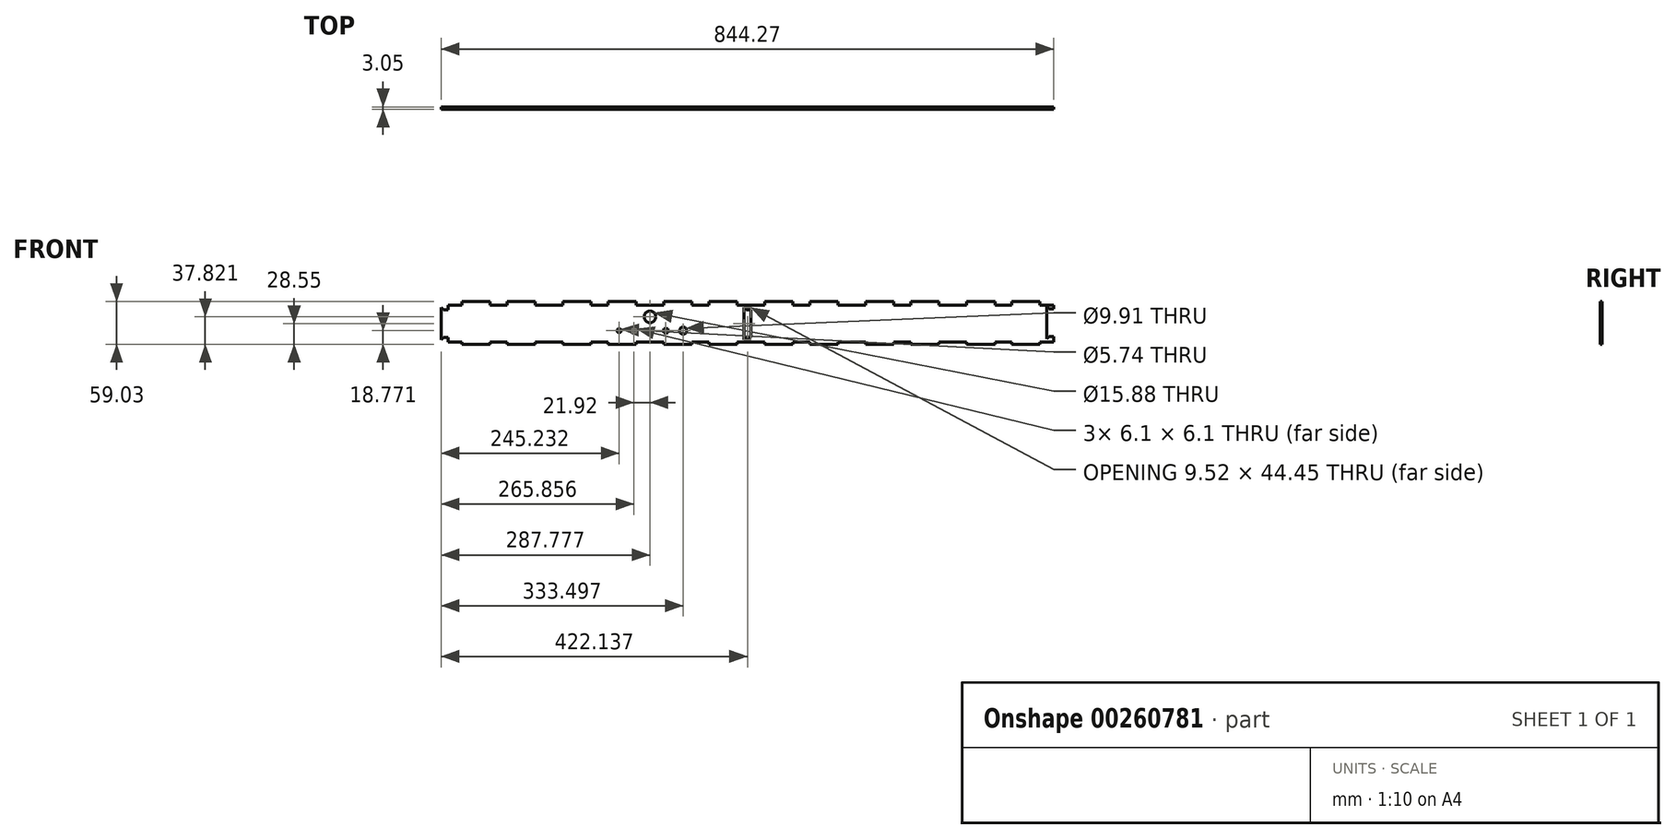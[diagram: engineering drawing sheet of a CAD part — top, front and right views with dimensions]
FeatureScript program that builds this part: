
annotation { "Feature Type Name" : "Feature", "Feature Type Description" : "" }
export const myFeature = defineFeature(function(context is Context, id is Id, definition is map)
    precondition{}
    {
        {
            var Q0;
            Q0=qCreatedBy(makeId("Front.planeOp"),FACE);
            var sketch = newSketch(context, id + "F0", { "sketchPlane" : qUnion([Q0])});
            skLineSegment(sketch, "E0.bottom", {"start": v(0, 0) * mm, "end": v(834.74, 0) * mm});
            skLineSegment(sketch, "E0.top", {"start": v(0, 50.8) * mm, "end": v(834.74, 50.8) * mm});
            skLineSegment(sketch, "E0.left", {"start": v(0, 0) * mm, "end": v(0, 50.8) * mm});
            skLineSegment(sketch, "E0.right", {"start": v(834.74, 0) * mm, "end": v(834.74, 50.8) * mm});
            skLineSegment(sketch, "E1", {"start": v(57.92, 50.8) * mm, "end": v(57.92, 0) * mm, "construction": true});
            skLineSegment(sketch, "E2", {"start": v(75.88, 50.8) * mm, "end": v(75.88, 0) * mm, "construction": true});
            skLineSegment(sketch, "E3", {"start": v(776.82, 50.8) * mm, "end": v(776.82, 0) * mm, "construction": true});
            skLineSegment(sketch, "E4", {"start": v(758.86, 50.8) * mm, "end": v(758.86, 0) * mm, "construction": true});
            skSolve(sketch);
        }
        {
            var Q0;
            Q0=makeQuery(id+"F0.imprint","IMPRINT",FACE,{"disambiguationData":[TD([[makeQuery(id+"F0.imprint","IMPRINT",EDGE,{"derivedFrom":sQuery(id+"F0.wireOp",EDGE,"E0.bottom")}),1.0]])]});
            extrude(context, id + "F1", {"entities" : qUnion([Q0]), "depth" : 3.05 * mm});
        }
        {
            var Q0;
            Q0=makeQuery(id+"F1.opExtrude","CAP_FACE",FACE,{"disambiguationData":[OSD([sQuery(id+"F0.wireOp",EDGE,"E0.bottom"),sQuery(id+"F0.wireOp",EDGE,"E0.top"),sQuery(id+"F0.wireOp",EDGE,"E0.left"),sQuery(id+"F0.wireOp",EDGE,"E0.right")])],"isStart":false});
            var sketch = newSketch(context, id + "F2", { "sketchPlane" : qUnion([Q0])});
            skLineSegment(sketch, "E5", {"start": v(57.92, 0) * mm, "end": v(57.92, 50.8) * mm});
            skLineSegment(sketch, "E6", {"start": v(81.2, 0) * mm, "end": v(81.2, 50.8) * mm});
            skLineSegment(sketch, "E7", {"start": v(776.82, 0) * mm, "end": v(776.82, 50.8) * mm});
            skLineSegment(sketch, "E8", {"start": v(753.54, 0) * mm, "end": v(753.54, 50.8) * mm});
            skLineSegment(sketch, "E9", {"start": v(197.05, 50.8) * mm, "end": v(197.05, 0) * mm});
            skLineSegment(sketch, "E10", {"start": v(220.32, 0) * mm, "end": v(220.32, 50.8) * mm});
            skLineSegment(sketch, "E11", {"start": v(336.17, 50.8) * mm, "end": v(336.17, 0) * mm});
            skLineSegment(sketch, "E12", {"start": v(359.45, 0.94) * mm, "end": v(359.45, 50.8) * mm});
            skLineSegment(sketch, "E13", {"start": v(475.3, 0) * mm, "end": v(475.3, 50.8) * mm});
            skLineSegment(sketch, "E14", {"start": v(498.57, 0) * mm, "end": v(498.57, 50.8) * mm});
            skLineSegment(sketch, "E15", {"start": v(614.42, 50.8) * mm, "end": v(614.42, 0) * mm});
            skLineSegment(sketch, "E16", {"start": v(637.7, 50.8) * mm, "end": v(637.7, 0) * mm});
            skCircle(sketch, "E17", {"center": v(9.53, 25.4) * mm, "radius": 1.27 * mm});
            skPoint(sketch, "E17.centerSnap0", {"position": v(0, 25.4) * mm});
            skCircle(sketch, "E18", {"center": v(825.22, 25.4) * mm, "radius": 1.27 * mm});
            skSolve(sketch);
        }
        {
            var Q0;
            {var subQ0=sQuery(id+"F2.wireOp",EDGE,"E6");Q0=makeQuery(id+"F2.imprint","IMPRINT",FACE,{"disambiguationData":[TD([[makeQuery(id+"F2.imprint","IMPRINT",EDGE,{"derivedFrom":subQ0}),-1.0]])]});}
            var sketch = newSketch(context, id + "F3", { "sketchPlane" : qUnion([Q0])});
            skLineSegment(sketch, "E19", {"start": v(0, 25.4) * mm, "end": v(834.74, 25.4) * mm, "construction": true});
            skLineSegment(sketch, "E20", {"start": v(0, 50.8) * mm, "end": v(0, 55.88) * mm});
            skLineSegment(sketch, "E21", {"start": v(0, 55.88) * mm, "end": v(57.92, 55.88) * mm});
            skLineSegment(sketch, "E22", {"start": v(57.92, 55.88) * mm, "end": v(57.92, 50.8) * mm});
            skLineSegment(sketch, "E23", {"start": v(81.2, 50.8) * mm, "end": v(81.2, 55.88) * mm});
            skLineSegment(sketch, "E24", {"start": v(81.2, 55.88) * mm, "end": v(197.05, 55.88) * mm});
            skLineSegment(sketch, "E25", {"start": v(197.05, 55.88) * mm, "end": v(197.05, 50.8) * mm});
            skLineSegment(sketch, "E26", {"start": v(220.32, 50.8) * mm, "end": v(220.32, 55.88) * mm});
            skLineSegment(sketch, "E27", {"start": v(220.32, 55.88) * mm, "end": v(336.17, 55.88) * mm});
            skLineSegment(sketch, "E28", {"start": v(336.17, 55.88) * mm, "end": v(336.17, 50.8) * mm});
            skLineSegment(sketch, "E29", {"start": v(359.45, 50.8) * mm, "end": v(359.45, 55.88) * mm});
            skLineSegment(sketch, "E30", {"start": v(359.45, 55.88) * mm, "end": v(475.3, 55.88) * mm});
            skLineSegment(sketch, "E31", {"start": v(475.3, 55.88) * mm, "end": v(475.3, 50.8) * mm});
            skLineSegment(sketch, "E32", {"start": v(498.57, 50.8) * mm, "end": v(498.57, 55.88) * mm});
            skLineSegment(sketch, "E33", {"start": v(498.57, 55.88) * mm, "end": v(614.42, 55.88) * mm});
            skLineSegment(sketch, "E34", {"start": v(614.42, 55.88) * mm, "end": v(614.42, 50.8) * mm});
            skLineSegment(sketch, "E35", {"start": v(637.7, 50.8) * mm, "end": v(637.7, 55.88) * mm});
            skLineSegment(sketch, "E36", {"start": v(637.7, 55.88) * mm, "end": v(753.54, 55.88) * mm});
            skLineSegment(sketch, "E37", {"start": v(753.54, 55.88) * mm, "end": v(753.54, 50.8) * mm});
            skLineSegment(sketch, "E38", {"start": v(776.82, 50.8) * mm, "end": v(776.82, 55.88) * mm});
            skLineSegment(sketch, "E39", {"start": v(776.82, 55.88) * mm, "end": v(834.74, 55.88) * mm});
            skLineSegment(sketch, "E40", {"start": v(834.74, 55.88) * mm, "end": v(834.74, 50.8) * mm});
            skLineSegment(sketch, "E41", {"start": v(0, 50.8) * mm, "end": v(834.74, 50.8) * mm});
            skLineSegment(sketch, "E42.bottom", {"start": v(0, 0) * mm, "end": v(57.92, 0) * mm});
            skLineSegment(sketch, "E42.top", {"start": v(0, -3.15) * mm, "end": v(57.92, -3.15) * mm});
            skLineSegment(sketch, "E42.left", {"start": v(0, 0) * mm, "end": v(0, -3.15) * mm});
            skLineSegment(sketch, "E42.right", {"start": v(57.92, 0) * mm, "end": v(57.92, -3.15) * mm});
            skLineSegment(sketch, "E43.bottom", {"start": v(81.2, 0) * mm, "end": v(197.05, 0) * mm});
            skLineSegment(sketch, "E43.top", {"start": v(81.2, -3.15) * mm, "end": v(197.05, -3.15) * mm});
            skLineSegment(sketch, "E43.left", {"start": v(81.2, 0) * mm, "end": v(81.2, -3.15) * mm});
            skLineSegment(sketch, "E43.right", {"start": v(197.05, 0) * mm, "end": v(197.05, -3.15) * mm});
            skLineSegment(sketch, "E44.bottom", {"start": v(220.32, 0) * mm, "end": v(336.17, 0) * mm});
            skLineSegment(sketch, "E44.top", {"start": v(220.32, -3.15) * mm, "end": v(336.17, -3.15) * mm});
            skLineSegment(sketch, "E44.left", {"start": v(220.32, 0) * mm, "end": v(220.32, -3.15) * mm});
            skLineSegment(sketch, "E44.right", {"start": v(336.17, 0) * mm, "end": v(336.17, -3.15) * mm});
            skLineSegment(sketch, "E45.bottom", {"start": v(359.45, 0) * mm, "end": v(475.3, 0) * mm});
            skLineSegment(sketch, "E45.top", {"start": v(359.45, -3.15) * mm, "end": v(475.3, -3.15) * mm});
            skLineSegment(sketch, "E45.left", {"start": v(359.45, 0) * mm, "end": v(359.45, -3.15) * mm});
            skLineSegment(sketch, "E45.right", {"start": v(475.3, 0) * mm, "end": v(475.3, -3.15) * mm});
            skLineSegment(sketch, "E46.bottom", {"start": v(498.57, 0) * mm, "end": v(614.42, 0) * mm});
            skLineSegment(sketch, "E46.top", {"start": v(498.57, -3.15) * mm, "end": v(614.42, -3.15) * mm});
            skLineSegment(sketch, "E46.left", {"start": v(498.57, 0) * mm, "end": v(498.57, -3.15) * mm});
            skLineSegment(sketch, "E46.right", {"start": v(614.42, 0) * mm, "end": v(614.42, -3.15) * mm});
            skLineSegment(sketch, "E47.bottom", {"start": v(637.7, 0) * mm, "end": v(753.54, 0) * mm});
            skLineSegment(sketch, "E47.top", {"start": v(637.7, -3.15) * mm, "end": v(753.54, -3.15) * mm});
            skLineSegment(sketch, "E47.left", {"start": v(637.7, 0) * mm, "end": v(637.7, -3.15) * mm});
            skLineSegment(sketch, "E47.right", {"start": v(753.54, 0) * mm, "end": v(753.54, -3.15) * mm});
            skLineSegment(sketch, "E48.bottom", {"start": v(776.82, 0) * mm, "end": v(834.74, 0) * mm});
            skLineSegment(sketch, "E48.top", {"start": v(776.82, -3.15) * mm, "end": v(834.74, -3.15) * mm});
            skLineSegment(sketch, "E48.left", {"start": v(776.82, 0) * mm, "end": v(776.82, -3.15) * mm});
            skLineSegment(sketch, "E48.right", {"start": v(834.74, 0) * mm, "end": v(834.74, -3.15) * mm});
            skSolve(sketch);
        }
        {
            var Q0;
            {var subQ0=sQuery(id+"F3.wireOp",EDGE,"E20");Q0=makeQuery(id+"F3.imprint","IMPRINT",FACE,{"disambiguationData":[TD([[makeQuery(id+"F3.imprint","IMPRINT",EDGE,{"derivedFrom":subQ0}),-1.0]])]});}
            var Q1;
            {var subQ0=sQuery(id+"F3.wireOp",EDGE,"E23");Q1=makeQuery(id+"F3.imprint","IMPRINT",FACE,{"disambiguationData":[TD([[makeQuery(id+"F3.imprint","IMPRINT",EDGE,{"derivedFrom":subQ0}),-1.0]])]});}
            var Q2;
            {var subQ0=sQuery(id+"F3.wireOp",EDGE,"300d203a-4e24-4113-8f0b-c0bd62af7ee03.MirrorCS");Q2=makeQuery(id+"F3.imprint","IMPRINT",FACE,{"disambiguationData":[TD([[makeQuery(id+"F3.imprint","IMPRINT",EDGE,{"derivedFrom":subQ0}),1.0]])]});}
            var Q3;
            {var subQ0=sQuery(id+"F3.wireOp",EDGE,"300d203a-4e24-4113-8f0b-c0bd62af7ee06.MirrorCS");Q3=makeQuery(id+"F3.imprint","IMPRINT",FACE,{"disambiguationData":[TD([[makeQuery(id+"F3.imprint","IMPRINT",EDGE,{"derivedFrom":subQ0}),1.0]])]});}
            var Q4;
            {var subQ0=sQuery(id+"F3.wireOp",EDGE,"E26");Q4=makeQuery(id+"F3.imprint","IMPRINT",FACE,{"disambiguationData":[TD([[makeQuery(id+"F3.imprint","IMPRINT",EDGE,{"derivedFrom":subQ0}),-1.0]])]});}
            var Q5;
            {var subQ0=sQuery(id+"F3.wireOp",EDGE,"300d203a-4e24-4113-8f0b-c0bd62af7ee09.MirrorCS");Q5=makeQuery(id+"F3.imprint","IMPRINT",FACE,{"disambiguationData":[TD([[makeQuery(id+"F3.imprint","IMPRINT",EDGE,{"derivedFrom":subQ0}),1.0]])]});}
            var Q6;
            {var subQ0=sQuery(id+"F3.wireOp",EDGE,"E29");Q6=makeQuery(id+"F3.imprint","IMPRINT",FACE,{"disambiguationData":[TD([[makeQuery(id+"F3.imprint","IMPRINT",EDGE,{"derivedFrom":subQ0}),-1.0]])]});}
            var Q7;
            {var subQ0=sQuery(id+"F3.wireOp",EDGE,"300d203a-4e24-4113-8f0b-c0bd62af7ee05.MirrorCS");Q7=makeQuery(id+"F3.imprint","IMPRINT",FACE,{"disambiguationData":[TD([[makeQuery(id+"F3.imprint","IMPRINT",EDGE,{"derivedFrom":subQ0}),1.0]])]});}
            var Q8;
            {var subQ0=sQuery(id+"F3.wireOp",EDGE,"E32");Q8=makeQuery(id+"F3.imprint","IMPRINT",FACE,{"disambiguationData":[TD([[makeQuery(id+"F3.imprint","IMPRINT",EDGE,{"derivedFrom":subQ0}),-1.0]])]});}
            var Q9;
            {var subQ0=sQuery(id+"F3.wireOp",EDGE,"300d203a-4e24-4113-8f0b-c0bd62af7ee02.MirrorCS");Q9=makeQuery(id+"F3.imprint","IMPRINT",FACE,{"disambiguationData":[TD([[makeQuery(id+"F3.imprint","IMPRINT",EDGE,{"derivedFrom":subQ0}),1.0]])]});}
            var Q10;
            {var subQ0=sQuery(id+"F3.wireOp",EDGE,"E35");Q10=makeQuery(id+"F3.imprint","IMPRINT",FACE,{"disambiguationData":[TD([[makeQuery(id+"F3.imprint","IMPRINT",EDGE,{"derivedFrom":subQ0}),-1.0]])]});}
            var Q11;
            {var subQ0=sQuery(id+"F3.wireOp",EDGE,"300d203a-4e24-4113-8f0b-c0bd62af7ee00.MirrorCS");Q11=makeQuery(id+"F3.imprint","IMPRINT",FACE,{"disambiguationData":[TD([[makeQuery(id+"F3.imprint","IMPRINT",EDGE,{"derivedFrom":subQ0}),1.0]])]});}
            var Q12;
            {var subQ0=sQuery(id+"F3.wireOp",EDGE,"E38");Q12=makeQuery(id+"F3.imprint","IMPRINT",FACE,{"disambiguationData":[TD([[makeQuery(id+"F3.imprint","IMPRINT",EDGE,{"derivedFrom":subQ0}),-1.0]])]});}
            var Q13;
            {var subQ0=sQuery(id+"F3.wireOp",EDGE,"300d203a-4e24-4113-8f0b-c0bd62af7ee04.MirrorCS");Q13=makeQuery(id+"F3.imprint","IMPRINT",FACE,{"disambiguationData":[TD([[makeQuery(id+"F3.imprint","IMPRINT",EDGE,{"derivedFrom":subQ0}),1.0]])]});}
            var Q14;
            Q14=makeQuery(id+"F3.imprint","IMPRINT",FACE,{"disambiguationData":[TD([[makeQuery(id+"F3.imprint","IMPRINT",EDGE,{"derivedFrom":sQuery(id+"F3.wireOp",EDGE,"E42.bottom")}),-1.0]])]});
            var Q15;
            Q15=makeQuery(id+"F3.imprint","IMPRINT",FACE,{"disambiguationData":[TD([[makeQuery(id+"F3.imprint","IMPRINT",EDGE,{"derivedFrom":sQuery(id+"F3.wireOp",EDGE,"E43.bottom")}),-1.0]])]});
            var Q16;
            Q16=makeQuery(id+"F3.imprint","IMPRINT",FACE,{"disambiguationData":[TD([[makeQuery(id+"F3.imprint","IMPRINT",EDGE,{"derivedFrom":sQuery(id+"F3.wireOp",EDGE,"E44.bottom")}),-1.0]])]});
            var Q17;
            Q17=makeQuery(id+"F3.imprint","IMPRINT",FACE,{"disambiguationData":[TD([[makeQuery(id+"F3.imprint","IMPRINT",EDGE,{"derivedFrom":sQuery(id+"F3.wireOp",EDGE,"E45.bottom")}),-1.0]])]});
            var Q18;
            Q18=makeQuery(id+"F3.imprint","IMPRINT",FACE,{"disambiguationData":[TD([[makeQuery(id+"F3.imprint","IMPRINT",EDGE,{"derivedFrom":sQuery(id+"F3.wireOp",EDGE,"E46.bottom")}),-1.0]])]});
            var Q19;
            Q19=makeQuery(id+"F3.imprint","IMPRINT",FACE,{"disambiguationData":[TD([[makeQuery(id+"F3.imprint","IMPRINT",EDGE,{"derivedFrom":sQuery(id+"F3.wireOp",EDGE,"E47.bottom")}),-1.0]])]});
            var Q20;
            Q20=makeQuery(id+"F3.imprint","IMPRINT",FACE,{"disambiguationData":[TD([[makeQuery(id+"F3.imprint","IMPRINT",EDGE,{"derivedFrom":sQuery(id+"F3.wireOp",EDGE,"E48.bottom")}),-1.0]])]});
            extrude(context, id + "F4", {"entities" : qUnion([Q0, Q1, Q2, Q3, Q4, Q5, Q6, Q7, Q8, Q9, Q10, Q11, Q12, Q13, Q14, Q15, Q16, Q17, Q18, Q19, Q20]), "operationType" : NewBodyOperationType.ADD, "oppositeDirection" : true, "depth" : 3.05 * mm});
        }
        {
            var Q0;
            {var subQ0=sQuery(id+"F2.wireOp",EDGE,"E6");Q0=makeQuery(id+"F2.imprint","IMPRINT",FACE,{"disambiguationData":[TD([[makeQuery(id+"F2.imprint","IMPRINT",EDGE,{"derivedFrom":subQ0}),-1.0]])]});}
            var sketch = newSketch(context, id + "F5", { "sketchPlane" : qUnion([Q0])});
            skLineSegment(sketch, "E49", {"start": v(0, 6.35) * mm, "end": v(0, 44.45) * mm});
            skPoint(sketch, "E50", {"position": v(0, 25.4) * mm});
            skLineSegment(sketch, "E51", {"start": v(0, 44.45) * mm, "end": v(-6.35, 44.45) * mm});
            skLineSegment(sketch, "E52", {"start": v(0, 6.35) * mm, "end": v(-6.35, 6.35) * mm});
            skLineSegment(sketch, "E53", {"start": v(-6.35, 44.45) * mm, "end": v(-9.52, 47.63) * mm});
            skLineSegment(sketch, "E54", {"start": v(-6.35, 6.35) * mm, "end": v(-9.52, 3.18) * mm});
            skLineSegment(sketch, "E55", {"start": v(-9.52, 47.63) * mm, "end": v(-9.52, 3.18) * mm});
            skLineSegment(sketch, "E56", {"start": v(834.74, 7.32) * mm, "end": v(834.74, 45.42) * mm});
            skPoint(sketch, "E57", {"position": v(834.74, 26.37) * mm});
            skLineSegment(sketch, "E58", {"start": v(834.74, 45.42) * mm, "end": v(828.4, 45.42) * mm});
            skLineSegment(sketch, "E59", {"start": v(834.74, 7.32) * mm, "end": v(828.4, 7.32) * mm});
            skLineSegment(sketch, "E60", {"start": v(828.4, 45.42) * mm, "end": v(825.22, 48.6) * mm});
            skLineSegment(sketch, "E61", {"start": v(828.4, 7.32) * mm, "end": v(825.22, 4.14) * mm});
            skLineSegment(sketch, "E62", {"start": v(825.22, 48.6) * mm, "end": v(825.22, 4.14) * mm});
            skSolve(sketch);
        }
        {
            var Q0;
            Q0=makeQuery(id+"F5.imprint","IMPRINT",FACE,{"disambiguationData":[TD([[makeQuery(id+"F5.imprint","IMPRINT",EDGE,{"derivedFrom":sQuery(id+"F5.wireOp",EDGE,"E49")}),1.0]])]});
            extrude(context, id + "F6", {"entities" : qUnion([Q0]), "operationType" : NewBodyOperationType.ADD, "oppositeDirection" : true, "depth" : 3.05 * mm});
        }
        {
            var Q0;
            Q0=makeQuery(id+"F5.imprint","IMPRINT",FACE,{"disambiguationData":[TD([[makeQuery(id+"F5.imprint","IMPRINT",EDGE,{"derivedFrom":sQuery(id+"F5.wireOp",EDGE,"E56")}),1.0]])]});
            extrude(context, id + "F7", {"entities" : qUnion([Q0]), "operationType" : NewBodyOperationType.REMOVE, "endBound" : BoundingType.THROUGH_ALL, "oppositeDirection" : true, "depth" : 25.4 * mm});
        }
        {
            var Q0;
            {var subQ0=sQuery(id+"F2.wireOp",EDGE,"E11");Q0=makeQuery(id+"F2.imprint","IMPRINT",FACE,{"disambiguationData":[TD([[makeQuery(id+"F2.imprint","IMPRINT",EDGE,{"derivedFrom":subQ0}),1.0]])]});}
            var sketch = newSketch(context, id + "F8", { "sketchPlane" : qUnion([Q0])});
            skLineSegment(sketch, "E63", {"start": v(417.37, 6.35) * mm, "end": v(417.37, 44.45) * mm});
            skLineSegment(sketch, "E64", {"start": v(417.37, 44.45) * mm, "end": v(411.02, 44.45) * mm});
            skLineSegment(sketch, "E65", {"start": v(411.02, 44.45) * mm, "end": v(407.85, 47.63) * mm});
            skLineSegment(sketch, "E66", {"start": v(407.85, 47.63) * mm, "end": v(407.85, 3.18) * mm});
            skLineSegment(sketch, "E67", {"start": v(407.85, 3.17) * mm, "end": v(411.02, 6.35) * mm});
            skLineSegment(sketch, "E68", {"start": v(411.02, 6.35) * mm, "end": v(417.37, 6.35) * mm});
            skPoint(sketch, "E69", {"position": v(417.37, 25.4) * mm});
            skPoint(sketch, "E70", {"position": v(407.85, 25.4) * mm});
            skLineSegment(sketch, "E71", {"start": v(407.85, 25.4) * mm, "end": v(417.37, 25.4) * mm, "construction": true});
            skSolve(sketch);
        }
        {
            var Q0;
            {var subQ0=sQuery(id+"F2.wireOp",EDGE,"E10");Q0=makeQuery(id+"F2.imprint","IMPRINT",FACE,{"disambiguationData":[TD([[makeQuery(id+"F2.imprint","IMPRINT",EDGE,{"derivedFrom":subQ0}),-1.0]])]});}
            var sketch = newSketch(context, id + "F9", { "sketchPlane" : qUnion([Q0])});
            skLineSegment(sketch, "E72.bottom", {"start": v(245.23, 21.59) * mm, "end": v(311.27, 21.59) * mm, "construction": true});
            skLineSegment(sketch, "E72.top", {"start": v(245.23, 9.65) * mm, "end": v(311.27, 9.65) * mm, "construction": true});
            skLineSegment(sketch, "E72.left", {"start": v(245.23, 21.59) * mm, "end": v(245.23, 9.65) * mm, "construction": true});
            skLineSegment(sketch, "E72.right", {"start": v(311.27, 21.59) * mm, "end": v(311.27, 9.65) * mm, "construction": true});
            skPoint(sketch, "E73", {"position": v(278.25, 9.65) * mm});
            skLineSegment(sketch, "E74.bottom", {"start": v(253.28, 12.57) * mm, "end": v(259.37, 12.57) * mm});
            skLineSegment(sketch, "E74.top", {"start": v(253.28, 18.67) * mm, "end": v(259.37, 18.67) * mm});
            skLineSegment(sketch, "E74.left", {"start": v(253.28, 12.57) * mm, "end": v(253.28, 18.67) * mm});
            skLineSegment(sketch, "E74.right", {"start": v(259.37, 12.57) * mm, "end": v(259.37, 18.67) * mm});
            skLineSegment(sketch, "E75.bottom", {"start": v(275.2, 12.57) * mm, "end": v(281.3, 12.57) * mm});
            skLineSegment(sketch, "E75.top", {"start": v(275.2, 18.67) * mm, "end": v(281.3, 18.67) * mm});
            skLineSegment(sketch, "E75.left", {"start": v(275.2, 12.57) * mm, "end": v(275.2, 18.67) * mm});
            skLineSegment(sketch, "E75.right", {"start": v(281.3, 12.57) * mm, "end": v(281.3, 18.67) * mm});
            skLineSegment(sketch, "E76.bottom", {"start": v(297.12, 12.57) * mm, "end": v(303.21, 12.57) * mm});
            skLineSegment(sketch, "E76.top", {"start": v(297.12, 18.67) * mm, "end": v(303.21, 18.67) * mm});
            skLineSegment(sketch, "E76.left", {"start": v(297.12, 12.57) * mm, "end": v(297.12, 18.67) * mm});
            skLineSegment(sketch, "E76.right", {"start": v(303.21, 12.57) * mm, "end": v(303.21, 18.67) * mm});
            skPoint(sketch, "E77", {"position": v(253.28, 15.62) * mm});
            skPoint(sketch, "E78", {"position": v(245.23, 15.62) * mm});
            skPoint(sketch, "E79", {"position": v(278.25, 18.67) * mm});
            skPoint(sketch, "E80", {"position": v(275.2, 15.62) * mm});
            skPoint(sketch, "E81", {"position": v(297.12, 15.62) * mm});
            skPoint(sketch, "E82", {"position": v(300.17, 18.67) * mm});
            skCircle(sketch, "E83", {"center": v(235.7, 15.62) * mm, "radius": 2.87 * mm});
            skCircle(sketch, "E84", {"center": v(323.97, 15.62) * mm, "radius": 4.95 * mm});
            skCircle(sketch, "E85", {"center": v(278.25, 34.67) * mm, "radius": 7.94 * mm});
            skSolve(sketch);
        }
        {
            var Q0;
            Q0=qSketchRegion(id+"F9",true);
            extrude(context, id + "F10", {"entities" : qUnion([Q0]), "operationType" : NewBodyOperationType.REMOVE, "endBound" : BoundingType.THROUGH_ALL, "oppositeDirection" : true, "depth" : 25.4 * mm});
        }
        {
            var Q0;
            Q0 = qSketchRegion(id + "F8", true);
            extrude(context, id + "F11", {"entities" : qUnion([Q0]), "operationType" : NewBodyOperationType.REMOVE, "oppositeDirection" : true, "depth" : 25.4 * mm});
        }
        {
            var Q0;
            {var subQ0=sQuery(id+"F2.wireOp",EDGE,"E6");Q0=makeQuery(id+"F2.imprint","IMPRINT",FACE,{"disambiguationData":[TD([[makeQuery(id+"F2.imprint","IMPRINT",EDGE,{"derivedFrom":subQ0}),-1.0]])]});}
            var sketch = newSketch(context, id + "F12", { "sketchPlane" : qUnion([Q0])});
            skLineSegment(sketch, "E86.bottom", {"start": v(158.17, -3.15) * mm, "end": v(120.07, -3.15) * mm});
            skLineSegment(sketch, "E86.top", {"start": v(158.17, -0.1) * mm, "end": v(120.07, -0.1) * mm});
            skLineSegment(sketch, "E86.left", {"start": v(158.17, -3.15) * mm, "end": v(158.17, -0.1) * mm});
            skLineSegment(sketch, "E86.right", {"start": v(120.07, -3.15) * mm, "end": v(120.07, -0.1) * mm});
            skLineSegment(sketch, "E87.bottom", {"start": v(259.2, -3.15) * mm, "end": v(297.3, -3.15) * mm});
            skLineSegment(sketch, "E87.top", {"start": v(259.2, -0.1) * mm, "end": v(297.3, -0.1) * mm});
            skLineSegment(sketch, "E87.left", {"start": v(259.2, -3.15) * mm, "end": v(259.2, -0.1) * mm});
            skLineSegment(sketch, "E87.right", {"start": v(297.3, -3.15) * mm, "end": v(297.3, -0.1) * mm});
            skLineSegment(sketch, "E88.bottom", {"start": v(398.32, -3.15) * mm, "end": v(436.42, -3.15) * mm});
            skLineSegment(sketch, "E88.top", {"start": v(398.32, -0.1) * mm, "end": v(436.42, -0.1) * mm});
            skLineSegment(sketch, "E88.left", {"start": v(398.32, -3.15) * mm, "end": v(398.32, -0.1) * mm});
            skLineSegment(sketch, "E88.right", {"start": v(436.42, -3.15) * mm, "end": v(436.42, -0.1) * mm});
            skLineSegment(sketch, "E89.bottom", {"start": v(537.44, -3.15) * mm, "end": v(575.54, -3.15) * mm});
            skLineSegment(sketch, "E89.top", {"start": v(537.44, -0.1) * mm, "end": v(575.54, -0.1) * mm});
            skLineSegment(sketch, "E89.left", {"start": v(537.44, -3.15) * mm, "end": v(537.44, -0.1) * mm});
            skLineSegment(sketch, "E89.right", {"start": v(575.54, -3.15) * mm, "end": v(575.54, -0.1) * mm});
            skLineSegment(sketch, "E90.bottom", {"start": v(676.57, -3.15) * mm, "end": v(714.67, -3.15) * mm});
            skLineSegment(sketch, "E90.top", {"start": v(676.57, -0.1) * mm, "end": v(714.67, -0.1) * mm});
            skLineSegment(sketch, "E90.left", {"start": v(676.57, -3.15) * mm, "end": v(676.57, -0.1) * mm});
            skLineSegment(sketch, "E90.right", {"start": v(714.67, -3.15) * mm, "end": v(714.67, -0.1) * mm});
            skLineSegment(sketch, "E91.bottom", {"start": v(815.7, -3.15) * mm, "end": v(853.8, -3.15) * mm});
            skLineSegment(sketch, "E91.top", {"start": v(815.7, -0.1) * mm, "end": v(853.8, -0.1) * mm});
            skLineSegment(sketch, "E91.left", {"start": v(815.7, -3.15) * mm, "end": v(815.7, -0.1) * mm});
            skLineSegment(sketch, "E91.right", {"start": v(853.8, -3.15) * mm, "end": v(853.8, -0.1) * mm});
            skLineSegment(sketch, "E92.bottom", {"start": v(19.05, -3.15) * mm, "end": v(-19.05, -3.15) * mm});
            skLineSegment(sketch, "E92.top", {"start": v(19.05, -0.1) * mm, "end": v(-19.05, -0.1) * mm});
            skLineSegment(sketch, "E92.left", {"start": v(19.05, -3.15) * mm, "end": v(19.05, -0.1) * mm});
            skLineSegment(sketch, "E92.right", {"start": v(-19.05, -3.15) * mm, "end": v(-19.05, -0.1) * mm});
            skPoint(sketch, "E93", {"position": v(139.12, -3.15) * mm});
            skPoint(sketch, "E94", {"position": v(278.25, -3.15) * mm});
            skPoint(sketch, "E95", {"position": v(417.37, -3.15) * mm});
            skPoint(sketch, "E96", {"position": v(556.5, -3.15) * mm});
            skPoint(sketch, "E97", {"position": v(695.62, -3.15) * mm});
            skPoint(sketch, "E98", {"position": v(0, -3.15) * mm});
            skPoint(sketch, "E99", {"position": v(834.74, -3.15) * mm});
            skLineSegment(sketch, "E100.bottom", {"start": v(-19.05, 55.88) * mm, "end": v(19.05, 55.88) * mm});
            skLineSegment(sketch, "E100.top", {"start": v(-19.05, 50.8) * mm, "end": v(19.05, 50.8) * mm});
            skLineSegment(sketch, "E100.left", {"start": v(-19.05, 55.88) * mm, "end": v(-19.05, 50.8) * mm});
            skLineSegment(sketch, "E100.right", {"start": v(19.05, 55.88) * mm, "end": v(19.05, 50.8) * mm});
            skLineSegment(sketch, "E101.bottom", {"start": v(120.07, 55.88) * mm, "end": v(158.17, 55.88) * mm});
            skLineSegment(sketch, "E101.top", {"start": v(120.07, 50.8) * mm, "end": v(158.17, 50.8) * mm});
            skLineSegment(sketch, "E101.left", {"start": v(120.07, 55.88) * mm, "end": v(120.07, 50.8) * mm});
            skLineSegment(sketch, "E101.right", {"start": v(158.17, 55.88) * mm, "end": v(158.17, 50.8) * mm});
            skLineSegment(sketch, "E102.bottom", {"start": v(259.2, 55.88) * mm, "end": v(297.3, 55.88) * mm});
            skLineSegment(sketch, "E102.top", {"start": v(259.2, 50.8) * mm, "end": v(297.3, 50.8) * mm});
            skLineSegment(sketch, "E102.left", {"start": v(259.2, 55.88) * mm, "end": v(259.2, 50.8) * mm});
            skLineSegment(sketch, "E102.right", {"start": v(297.3, 55.88) * mm, "end": v(297.3, 50.8) * mm});
            skLineSegment(sketch, "E103.bottom", {"start": v(398.32, 55.88) * mm, "end": v(436.42, 55.88) * mm});
            skLineSegment(sketch, "E103.top", {"start": v(398.32, 50.8) * mm, "end": v(436.42, 50.8) * mm});
            skLineSegment(sketch, "E103.left", {"start": v(398.32, 55.88) * mm, "end": v(398.32, 50.8) * mm});
            skLineSegment(sketch, "E103.right", {"start": v(436.42, 55.88) * mm, "end": v(436.42, 50.8) * mm});
            skLineSegment(sketch, "E104.bottom", {"start": v(537.44, 55.88) * mm, "end": v(575.54, 55.88) * mm});
            skLineSegment(sketch, "E104.top", {"start": v(537.44, 50.8) * mm, "end": v(575.54, 50.8) * mm});
            skLineSegment(sketch, "E104.left", {"start": v(537.44, 55.88) * mm, "end": v(537.44, 50.8) * mm});
            skLineSegment(sketch, "E104.right", {"start": v(575.54, 55.88) * mm, "end": v(575.54, 50.8) * mm});
            skLineSegment(sketch, "E105.bottom", {"start": v(676.57, 55.88) * mm, "end": v(714.67, 55.88) * mm});
            skLineSegment(sketch, "E105.top", {"start": v(676.57, 50.8) * mm, "end": v(714.67, 50.8) * mm});
            skLineSegment(sketch, "E105.left", {"start": v(676.57, 55.88) * mm, "end": v(676.57, 50.8) * mm});
            skLineSegment(sketch, "E105.right", {"start": v(714.67, 55.88) * mm, "end": v(714.67, 50.8) * mm});
            skLineSegment(sketch, "E106.bottom", {"start": v(815.7, 55.88) * mm, "end": v(853.8, 55.88) * mm});
            skLineSegment(sketch, "E106.top", {"start": v(815.7, 50.8) * mm, "end": v(853.8, 50.8) * mm});
            skLineSegment(sketch, "E106.left", {"start": v(815.7, 55.88) * mm, "end": v(815.7, 50.8) * mm});
            skLineSegment(sketch, "E106.right", {"start": v(853.8, 55.88) * mm, "end": v(853.8, 50.8) * mm});
            skPoint(sketch, "E107", {"position": v(834.74, 55.88) * mm});
            skPoint(sketch, "E108", {"position": v(695.62, 55.88) * mm});
            skPoint(sketch, "E109", {"position": v(556.5, 55.88) * mm});
            skPoint(sketch, "E110", {"position": v(417.37, 55.88) * mm});
            skPoint(sketch, "E111", {"position": v(278.25, 55.88) * mm});
            skPoint(sketch, "E112", {"position": v(139.12, 55.88) * mm});
            skPoint(sketch, "E113", {"position": v(0, 55.88) * mm});
            skSolve(sketch);
        }
        {
            var Q0;
            Q0 = qSketchRegion(id + "F12", true);
            var Q1;
            {var subQ0=sQuery(id+"F3.wireOp",EDGE,"E41");Q1=makeQuery(id+"F6.boolean.opBoolean","MERGE",FACE,{"derivedFrom":[makeQuery(id+"F4.boolean.opBoolean","MERGE",FACE,{"derivedFrom":[makeQuery(id+"F1.opExtrude","CAP_FACE",FACE,{"disambiguationData":[OSD([sQuery(id+"F0.wireOp",EDGE,"E0.bottom"),sQuery(id+"F0.wireOp",EDGE,"E0.top"),sQuery(id+"F0.wireOp",EDGE,"E0.left"),sQuery(id+"F0.wireOp",EDGE,"E0.right")])],"isStart":true}),makeQuery(id+"F4.opExtrude","CAP_FACE",FACE,{"disambiguationData":[OSD([sQuery(id+"F3.wireOp",EDGE,"E20"),sQuery(id+"F3.wireOp",EDGE,"E21"),sQuery(id+"F3.wireOp",EDGE,"E22"),subQ0])],"isStart":false}),makeQuery(id+"F4.opExtrude","CAP_FACE",FACE,{"disambiguationData":[OSD([sQuery(id+"F3.wireOp",EDGE,"E23"),sQuery(id+"F3.wireOp",EDGE,"E24"),sQuery(id+"F3.wireOp",EDGE,"E25"),subQ0])],"isStart":false}),makeQuery(id+"F4.opExtrude","CAP_FACE",FACE,{"disambiguationData":[OSD([sQuery(id+"F3.wireOp",EDGE,"E26"),sQuery(id+"F3.wireOp",EDGE,"E27"),sQuery(id+"F3.wireOp",EDGE,"E28"),subQ0])],"isStart":false}),makeQuery(id+"F4.opExtrude","CAP_FACE",FACE,{"disambiguationData":[OSD([sQuery(id+"F3.wireOp",EDGE,"E29"),sQuery(id+"F3.wireOp",EDGE,"E30"),sQuery(id+"F3.wireOp",EDGE,"E31"),subQ0])],"isStart":false}),makeQuery(id+"F4.opExtrude","CAP_FACE",FACE,{"disambiguationData":[OSD([sQuery(id+"F3.wireOp",EDGE,"E32"),sQuery(id+"F3.wireOp",EDGE,"E33"),sQuery(id+"F3.wireOp",EDGE,"E34"),subQ0])],"isStart":false}),makeQuery(id+"F4.opExtrude","CAP_FACE",FACE,{"disambiguationData":[OSD([sQuery(id+"F3.wireOp",EDGE,"E35"),sQuery(id+"F3.wireOp",EDGE,"E36"),sQuery(id+"F3.wireOp",EDGE,"E37"),subQ0])],"isStart":false}),makeQuery(id+"F4.opExtrude","CAP_FACE",FACE,{"disambiguationData":[OSD([sQuery(id+"F3.wireOp",EDGE,"E38"),sQuery(id+"F3.wireOp",EDGE,"E39"),sQuery(id+"F3.wireOp",EDGE,"E40"),subQ0])],"isStart":false}),makeQuery(id+"F4.opExtrude","CAP_FACE",FACE,{"disambiguationData":[OSD([sQuery(id+"F3.wireOp",EDGE,"E42.bottom"),sQuery(id+"F3.wireOp",EDGE,"E42.top"),sQuery(id+"F3.wireOp",EDGE,"E42.left"),sQuery(id+"F3.wireOp",EDGE,"E42.right")])],"isStart":false}),makeQuery(id+"F4.opExtrude","CAP_FACE",FACE,{"disambiguationData":[OSD([sQuery(id+"F3.wireOp",EDGE,"E43.bottom"),sQuery(id+"F3.wireOp",EDGE,"E43.top"),sQuery(id+"F3.wireOp",EDGE,"E43.left"),sQuery(id+"F3.wireOp",EDGE,"E43.right")])],"isStart":false}),makeQuery(id+"F4.opExtrude","CAP_FACE",FACE,{"disambiguationData":[OSD([sQuery(id+"F3.wireOp",EDGE,"E44.bottom"),sQuery(id+"F3.wireOp",EDGE,"E44.top"),sQuery(id+"F3.wireOp",EDGE,"E44.left"),sQuery(id+"F3.wireOp",EDGE,"E44.right")])],"isStart":false}),makeQuery(id+"F4.opExtrude","CAP_FACE",FACE,{"disambiguationData":[OSD([sQuery(id+"F3.wireOp",EDGE,"E45.bottom"),sQuery(id+"F3.wireOp",EDGE,"E45.top"),sQuery(id+"F3.wireOp",EDGE,"E45.left"),sQuery(id+"F3.wireOp",EDGE,"E45.right")])],"isStart":false}),makeQuery(id+"F4.opExtrude","CAP_FACE",FACE,{"disambiguationData":[OSD([sQuery(id+"F3.wireOp",EDGE,"E46.bottom"),sQuery(id+"F3.wireOp",EDGE,"E46.top"),sQuery(id+"F3.wireOp",EDGE,"E46.left"),sQuery(id+"F3.wireOp",EDGE,"E46.right")])],"isStart":false}),makeQuery(id+"F4.opExtrude","CAP_FACE",FACE,{"disambiguationData":[OSD([sQuery(id+"F3.wireOp",EDGE,"E47.bottom"),sQuery(id+"F3.wireOp",EDGE,"E47.top"),sQuery(id+"F3.wireOp",EDGE,"E47.left"),sQuery(id+"F3.wireOp",EDGE,"E47.right")])],"isStart":false}),makeQuery(id+"F4.opExtrude","CAP_FACE",FACE,{"disambiguationData":[OSD([sQuery(id+"F3.wireOp",EDGE,"E48.bottom"),sQuery(id+"F3.wireOp",EDGE,"E48.top"),sQuery(id+"F3.wireOp",EDGE,"E48.left"),sQuery(id+"F3.wireOp",EDGE,"E48.right")])],"isStart":false})]}),makeQuery(id+"F6.opExtrude","CAP_FACE",FACE,{"disambiguationData":[OSD([sQuery(id+"F5.wireOp",EDGE,"E49"),sQuery(id+"F5.wireOp",EDGE,"E51"),sQuery(id+"F5.wireOp",EDGE,"E52"),sQuery(id+"F5.wireOp",EDGE,"E53"),sQuery(id+"F5.wireOp",EDGE,"E54"),sQuery(id+"F5.wireOp",EDGE,"E55")])],"isStart":false})]});}
            extrude(context, id + "F13", {"entities" : qUnion([Q0]), "operationType" : NewBodyOperationType.REMOVE, "endBound" : BoundingType.UP_TO_SURFACE, "oppositeDirection" : true, "endBoundEntityFace" : qUnion([Q1]), "depth" : 25.4 * mm});
        }
    });
